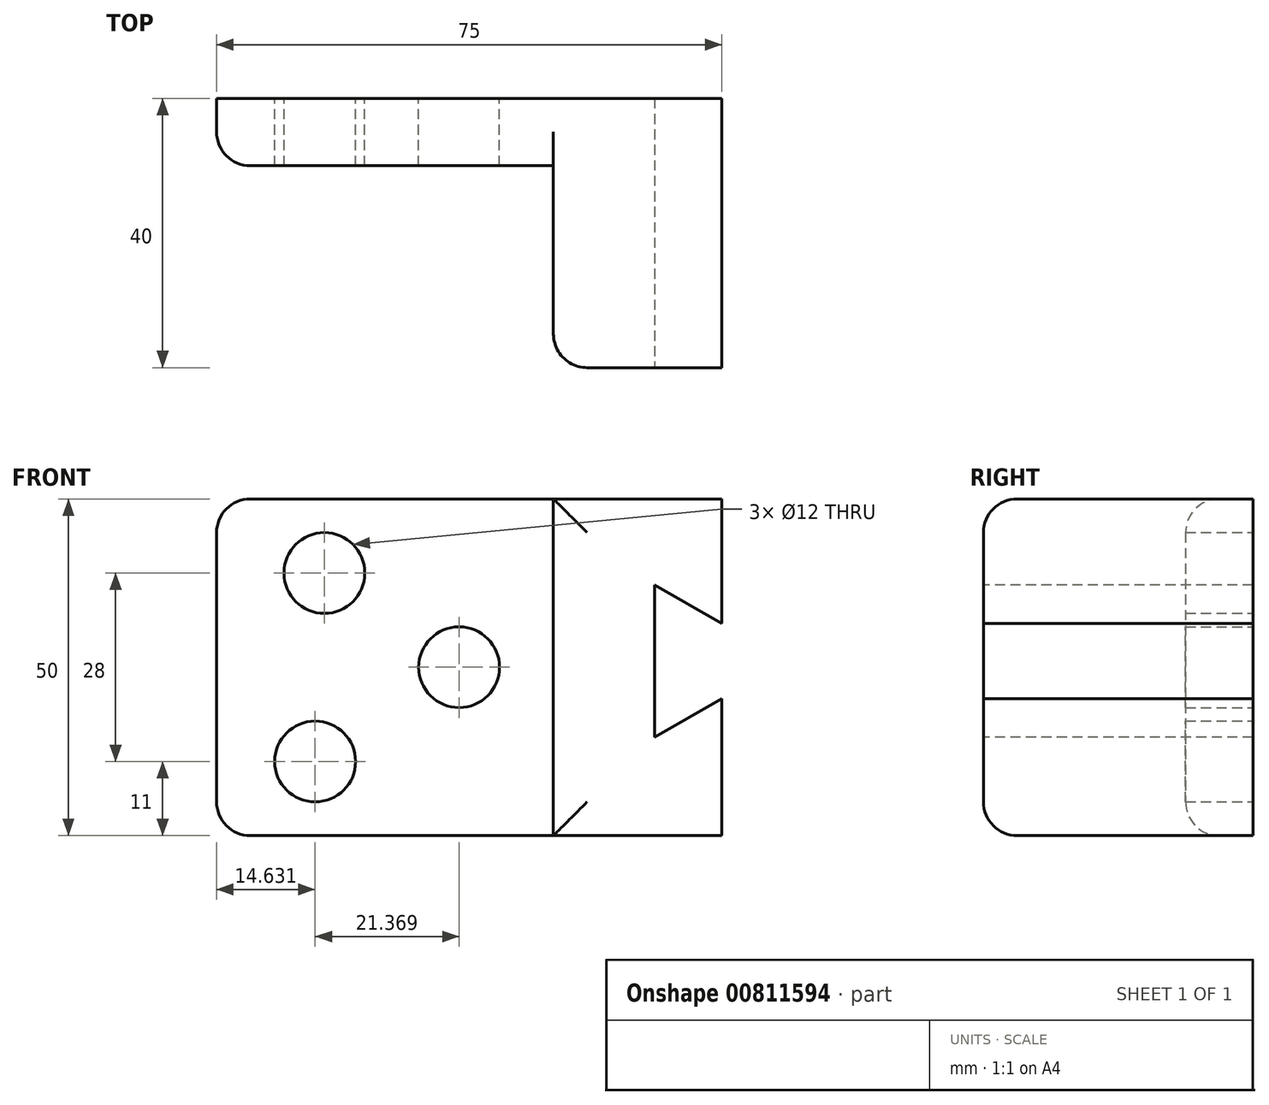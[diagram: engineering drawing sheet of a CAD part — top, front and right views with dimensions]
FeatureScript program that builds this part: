
annotation { "Feature Type Name" : "Feature", "Feature Type Description" : "" }
export const myFeature = defineFeature(function(context is Context, id is Id, definition is map)
    precondition{}
    {
        {
            var Q0;
            Q0=qCreatedBy(makeId("Front.planeOp"),FACE);
            var sketch = newSketch(context, id + "F0", { "sketchPlane" : qUnion([Q0])});
            skLineSegment(sketch, "E0.bottom", {"start": v(50, 25) * mm, "end": v(-50, 25) * mm});
            skLineSegment(sketch, "E0.top", {"start": v(50, -25) * mm, "end": v(-50, -25) * mm});
            skLineSegment(sketch, "E0.left", {"start": v(50, 25) * mm, "end": v(50, -25) * mm});
            skLineSegment(sketch, "E0.right", {"start": v(-50, 25) * mm, "end": v(-50, -25) * mm});
            skPoint(sketch, "E0.middle", {"position": v(0, 0) * mm});
            skLineSegment(sketch, "E1", {"start": v(0, 25) * mm, "end": v(0, -25) * mm, "construction": true});
            skLineSegment(sketch, "E2", {"start": v(-50, 0) * mm, "end": v(50, 0) * mm, "construction": true});
            skCircle(sketch, "E3", {"center": v(-35.37, -14) * mm, "radius": 6 * mm});
            skCircle(sketch, "E4", {"center": v(-34, 14) * mm, "radius": 6 * mm});
            skCircle(sketch, "E5", {"center": v(-14, 0) * mm, "radius": 6 * mm});
            skLineSegment(sketch, "E6", {"start": v(25, 25) * mm, "end": v(25, -25) * mm});
            skLineSegment(sketch, "E7", {"start": v(25, -25) * mm, "end": v(50, -25) * mm});
            skLineSegment(sketch, "E8", {"start": v(50, 25) * mm, "end": v(25, 25) * mm});
            skSolve(sketch);
        }
        {
            var Q0;
            {var subQ2=sQuery(id+"F0.wireOp",EDGE,"E0.right");Q0=makeQuery(id+"F0.imprint","IMPRINT",FACE,{"disambiguationData":[TD([[makeQuery(id+"F0.imprint","IMPRINT",EDGE,{"derivedFrom":subQ2}),1.0]])]});}
            extrude(context, id + "F1", {"entities" : qUnion([Q0]), "depth" : 10 * mm, "offsetDistance" : 25 * mm});
        }
        {
            var Q0;
            Q0=makeQuery(id+"F1.opExtrude","CAP_FACE",FACE,{"disambiguationData":[OSD([sQuery(id+"F0.wireOp",EDGE,"E0.bottom"),sQuery(id+"F0.wireOp",EDGE,"E0.top"),sQuery(id+"F0.wireOp",EDGE,"E0.right"),sQuery(id+"F0.wireOp",EDGE,"E3"),sQuery(id+"F0.wireOp",EDGE,"E4"),sQuery(id+"F0.wireOp",EDGE,"E5"),sQuery(id+"F0.wireOp",EDGE,"E6")])],"isStart":false});
            var sketch = newSketch(context, id + "F2", { "sketchPlane" : qUnion([Q0])});
            skLineSegment(sketch, "E9", {"start": v(0, 25) * mm, "end": v(0, -25) * mm});
            skLineSegment(sketch, "E10", {"start": v(0, -25) * mm, "end": v(25, -25) * mm});
            skLineSegment(sketch, "E11", {"start": v(25, -25) * mm, "end": v(25, 25) * mm});
            skLineSegment(sketch, "E12", {"start": v(25, 25) * mm, "end": v(0, 25) * mm});
            skSolve(sketch);
        }
        {
            var Q0;
            Q0 = qSketchRegion(id + "F2", true);
            extrude(context, id + "F3", {"entities" : qUnion([Q0]), "operationType" : NewBodyOperationType.ADD, "depth" : 30 * mm, "offsetDistance" : 25 * mm});
        }
        {
            var Q0;
            Q0=makeQuery(id+"F3.opExtrude","CAP_FACE",FACE,{"disambiguationData":[OSD([sQuery(id+"F2.wireOp",EDGE,"E9"),sQuery(id+"F2.wireOp",EDGE,"E10"),sQuery(id+"F2.wireOp",EDGE,"E11"),sQuery(id+"F2.wireOp",EDGE,"E12")])],"isStart":false});
            var sketch = newSketch(context, id + "F4", { "sketchPlane" : qUnion([Q0])});
            skLineSegment(sketch, "E13", {"start": v(25, 6.47) * mm, "end": v(15, 12.25) * mm});
            skLineSegment(sketch, "E14", {"start": v(15, 12.25) * mm, "end": v(15, -10.42) * mm});
            skLineSegment(sketch, "E15", {"start": v(15, -10.42) * mm, "end": v(25, -4.64) * mm});
            skLineSegment(sketch, "E16", {"start": v(25, -4.64) * mm, "end": v(25, 6.47) * mm});
            skSolve(sketch);
        }
        {
            var Q0;
            Q0 = qSketchRegion(id + "F4", true);
            extrude(context, id + "F5", {"entities" : qUnion([Q0]), "operationType" : NewBodyOperationType.REMOVE, "endBound" : BoundingType.THROUGH_ALL, "oppositeDirection" : true, "depth" : 25 * mm, "offsetDistance" : 25 * mm});
        }
        {
            var Q0;
            Q0=makeQuery(id+"F1.opExtrude","SWEPT_EDGE",EDGE,{"disambiguationData":[OSD([sQuery(id+"F0.wireOp",EDGE,"E0.top"),sQuery(id+"F0.wireOp",EDGE,"E0.right")])]});
            var Q1;
            Q1=makeQuery(id+"F1.opExtrude","SWEPT_EDGE",EDGE,{"disambiguationData":[OSD([sQuery(id+"F0.wireOp",EDGE,"E0.bottom"),sQuery(id+"F0.wireOp",EDGE,"E0.right")])]});
            var Q2;
            Q2=makeQuery(id+"F3.opExtrude","CAP_EDGE",EDGE,{"disambiguationData":[OSD([sQuery(id+"F2.wireOp",EDGE,"E9")])],"isStart":true});
            fillet(context, id + "F6", {"entities" : qUnion([Q0, Q1, Q2]), "radius" : 5 * mm, "tangentPropagation" : true, "allowEdgeOverflow" : false});
        }
        {
            var Q0;
            Q0=makeQuery(id+"F1.opExtrude","CAP_EDGE",EDGE,{"disambiguationData":[OSD([sQuery(id+"F0.wireOp",EDGE,"E0.top")])],"isStart":false});
            var Q1;
            Q1=makeQuery(id+"F3.opExtrude","CAP_EDGE",EDGE,{"disambiguationData":[OSD([sQuery(id+"F2.wireOp",EDGE,"E10")])],"isStart":false});
            var Q2;
            Q2=makeQuery(id+"F3.opExtrude","CAP_EDGE",EDGE,{"disambiguationData":[OSD([sQuery(id+"F2.wireOp",EDGE,"E9")])],"isStart":false});
            var Q3;
            Q3=makeQuery(id+"F3.opExtrude","CAP_EDGE",EDGE,{"disambiguationData":[OSD([sQuery(id+"F2.wireOp",EDGE,"E12")])],"isStart":false});
            fillet(context, id + "F7", {"entities" : qUnion([Q0, Q1, Q2, Q3]), "radius" : 5 * mm, "tangentPropagation" : true, "allowEdgeOverflow" : false});
        }
    });
